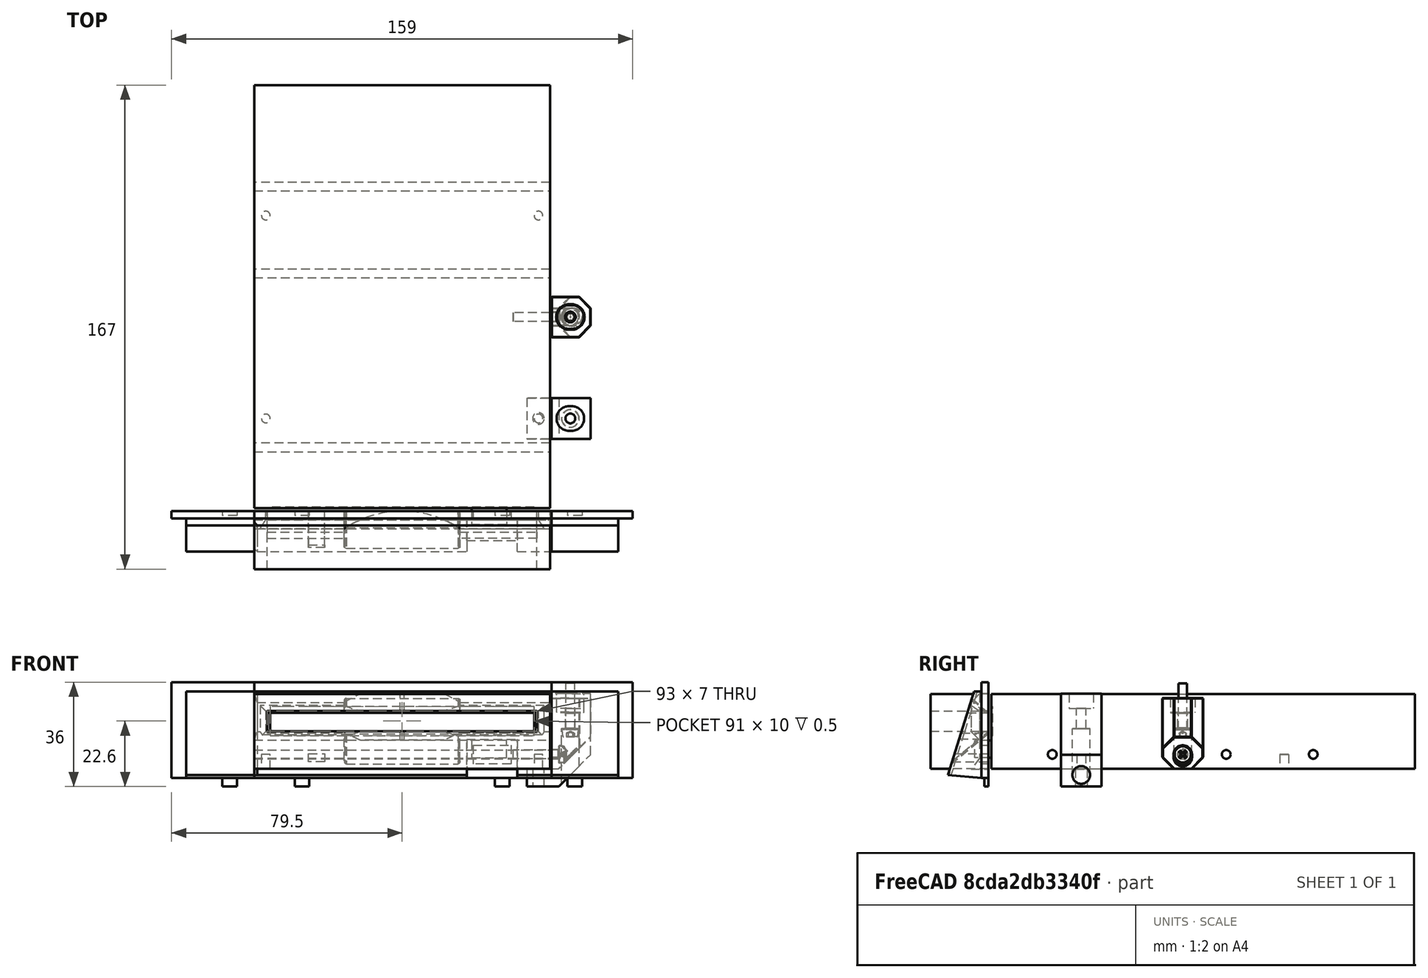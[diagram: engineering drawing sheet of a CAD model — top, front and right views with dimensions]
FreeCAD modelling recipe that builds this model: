
FCSTD DOCUMENT  (FreeCAD 0.21R33771 (Git))
Label: FDD
License: All rights reserved
LicenseURL: https://en.wikipedia.org/wiki/All_rights_reserved
objects: Sketcher::SketchObject×18, PartDesign::Pocket×10, Part::FeaturePython×8, PartDesign::Pad×6, PartDesign::Body×6, PartDesign::CoordinateSystem×6, PartDesign::Chamfer×6, PartDesign::Hole×3, PartDesign::LinearPattern×2, Part::Feature×2, PartDesign::Plane×2, App::DocumentObjectGroup×2, Mesh::Feature×1, PartDesign::FeatureBase×1
note: 95 computed .brp shape members not serialized (recipe doc carries the construction recipe); baked Part::Feature solids carry a one-line shape summary decoded from their .brp

FEATURE [Sketcher::SketchObject] Sketch  label="FloppyOutline"
  FullyConstrained = true
  MapMode = 5
  sketch-geometry (5):
    g0: LineSegment StartX=-51 StartY=73 StartZ=0 EndX=-51 EndY=-73 EndZ=0
    g1: LineSegment StartX=-51 StartY=-73 StartZ=0 EndX=51 EndY=-73 EndZ=0
    g2: LineSegment StartX=51 StartY=-73 StartZ=0 EndX=51 EndY=73 EndZ=0
    g3: LineSegment StartX=51 StartY=73 StartZ=0 EndX=-51 EndY=73 EndZ=0
    g4: GeomPoint X=0 Y=0 Z=0
  constraints (13):
    c: Coincident(g0,g1)
    c: Coincident(g1,g2)
    c: Coincident(g2,g3)
    c: Coincident(g3,g0)
    c: Vertical(g0)
    c: Vertical(g2)
    c: Horizontal(g1)
    c: Horizontal(g3)
    c: Symmetric(g2,g0,g4)
    c: Coincident(g4,g-1)
    c: DistanceX(g3,g3) = 102
    c: DistanceY(g2,g2) = 146
    c: Block(g2)
FEATURE [PartDesign::LinearPattern] LinearPattern
  Direction = -> X_Axis
  Length = 60
  Occurrences = 2
  Refine = true
  Reversed = true
FEATURE [PartDesign::LinearPattern] LinearPattern001
  BaseFeature = -> LinearPattern
  Direction = -> X_Axis
  Length = 90
  Occurrences = 2
  Refine = true
  Reversed = true
FEATURE [Sketcher::SketchObject] Sketch005
  AttachmentOffset = pos=(0,0,2) rot=(0,0,1;0rad)
  FullyConstrained = true
  MapMode = 5
  Placement = pos=(0,-2,-4e-16) rot=(1,0,0;1.5708rad)
  Support = -> [XZ_Plane001]
  sketch-geometry (7):
    g0: LineSegment StartX=43 StartY=-13 StartZ=0 EndX=43 EndY=-19 EndZ=0
    g1: LineSegment StartX=43 StartY=-19 StartZ=0 EndX=54 EndY=-19 EndZ=0
    g2: LineSegment StartX=54 StartY=-19 StartZ=0 EndX=65 EndY=-8 EndZ=0
    g3: LineSegment StartX=65 StartY=-8 StartZ=0 EndX=65 EndY=13 EndZ=0
    g4: LineSegment StartX=65 StartY=13 StartZ=0 EndX=51.5 EndY=13 EndZ=0
    g5: LineSegment StartX=51.5 StartY=13 StartZ=0 EndX=51.5 EndY=-13 EndZ=0
    g6: LineSegment StartX=51.5 StartY=-13 StartZ=0 EndX=43 EndY=-13 EndZ=0
  constraints (16):
    c: Coincident(g0,g1)
    c: Coincident(g3,g4)
    c: Coincident(g6,g0)
    c: Horizontal(g6)
    c: Parallel(g1,g-1)
    c: Coincident(g1,g2)
    c: Coincident(g4,g5)
    c: Coincident(g5,g6)
    c: Parallel(g4,g-1)
    c: Block(g5)
    c: Coincident(g2,g3)
    c: Angle(g-1,g2) = 0.785398
    c: Parallel(g3,g-2)
    c: Block(g4)
    c: Block(g2)
    c: Block(g0)
FEATURE [PartDesign::Pad] Pad002  label="Pad003"
  Direction = (0,-1,-2e-16)
  Length = 14
  Length2 = 10
  Midplane = true
  Placement = pos=(0,0,0) rot=(1,0,0;1.5708rad)
  Profile = -> Sketch005
  ReferenceAxis = -> Sketch005 [N_Axis]
  Refine = true
  Type = 0
FEATURE [Sketcher::SketchObject] Sketch007
  FullyConstrained = true
  MapMode = 5
  Placement = pos=(0,0,-19) rot=(1,0,0;3.14159rad)
  Support = -> [Pad002]
  sketch-geometry (1):
    g0: Circle CenterX=47 CenterY=2 CenterZ=0 NormalX=0 NormalY=0 NormalZ=1 AngleXU=0 Radius=2
  constraints (2):
    c: Block(g0)
    c: Diameter(g0) = 4
FEATURE [Sketcher::SketchObject] Sketch008
  FullyConstrained = true
  MapMode = 5
  Placement = pos=(2e-15,-3e-15,13) rot=(0,0,1;3.14159rad)
  sketch-geometry (4):
    g0: ArcOfCircle CenterX=-57.5013 CenterY=2 CenterZ=0 NormalX=0 NormalY=0 NormalZ=1 AngleXU=0 Radius=4.25 StartAngle=4.71239 EndAngle=7.85398
    g1: ArcOfCircle CenterX=-58.5 CenterY=2 CenterZ=0 NormalX=0 NormalY=0 NormalZ=1 AngleXU=0 Radius=4.25 StartAngle=1.5708 EndAngle=4.71239
    g2: LineSegment StartX=-57.5013 StartY=6.25 StartZ=0 EndX=-58.5 EndY=6.25 EndZ=0
    g3: LineSegment StartX=-58.5 StartY=-2.25 StartZ=0 EndX=-57.5013 EndY=-2.25 EndZ=0
  constraints (9):
    c: Tangent(g0,g2) = -1.5708
    c: Tangent(g2,g1) = -1.5708
    c: Tangent(g1,g3) = -1.5708
    c: Tangent(g3,g0) = -1.5708
    c: Equal(g0,g1)
    c: Horizontal(g2)
    c: Diameter(g1) = 8.5
    c: Block(g1)
    c: Block(g0)
FEATURE [PartDesign::Pocket] Pocket003
  BaseFeature = -> Pad002
  Direction = (0,0,-1)
  Length = 5
  Length2 = 5
  Placement = pos=(0,0,0) rot=(1,0,0;1.5708rad)
  Profile = -> Sketch008
  ReferenceAxis = -> Sketch008 [N_Axis]
  Refine = true
  Type = 0
FEATURE [Sketcher::SketchObject] Sketch009
  FullyConstrained = true
  MapMode = 5
  Placement = pos=(0,0,-19) rot=(1,0,0;3.14159rad)
  Support = -> [Pocket003]
  sketch-geometry (1):
    g0: Circle CenterX=58 CenterY=2 CenterZ=0 NormalX=0 NormalY=0 NormalZ=1 AngleXU=0 Radius=1.52384
  constraints (1):
    c: Block(g0)
FEATURE [PartDesign::Hole] Hole
  BaseFeature = -> Pocket003
  CustomThreadClearance = 0
  Depth = 81.8287
  DepthType = 1
  Diameter = 3.4
  DrillForDepth = false
  DrillPoint = 1
  DrillPointAngle = 118
  HoleCutCountersinkAngle = 90
  HoleCutCustomValues = false
  HoleCutDepth = 20
  HoleCutDiameter = 6.1
  HoleCutType = 1
  ModelThread = false
  Placement = pos=(0,0,0) rot=(1,0,0;1.5708rad)
  Profile = -> Sketch009
  Refine = true
  Tapered = false
  TaperedAngle = 90
  ThreadClass = 0
  ThreadDepth = 81.8287
  ThreadDepthType = 0
  ThreadDirection = 0
  ThreadFit = 0
  ThreadSize = 9
  ThreadType = 1
  Threaded = false
  UseCustomThreadClearance = false
FEATURE [PartDesign::Pocket] Pocket004  label="MountHole"
  BaseFeature = -> Hole
  Direction = (0,-2e-16,1)
  Length = 0
  Length2 = 5
  Placement = pos=(0,0,0) rot=(1,0,0;1.5708rad)
  Profile = -> Sketch007
  ReferenceAxis = -> Sketch007 [N_Axis]
  Refine = true
  Type = 2
FEATURE [PartDesign::Body] Body001  label="BottomBracket"
  Group = -> [Sketch005,Pad002,Sketch007,Sketch008,Pocket003,Sketch009,Hole,Pocket004]
  Origin = -> Origin001
  Placement = pos=(0,-40,0) rot=(0,0,1;0rad)
  Tip = -> Pocket004
FEATURE [PartDesign::Pad] Pad  label="FloppyCase"
  Direction = (0,0,1)
  Length = 25.8
  Length2 = 10
  Midplane = true
  Profile = -> Sketch
  ReferenceAxis = -> Sketch [N_Axis]
  Refine = true
  Type = 0
FEATURE [Sketcher::SketchObject] Sketch003  label="EjectSketch"
  FullyConstrained = true
  MapMode = 5
  Placement = pos=(0,-73,0) rot=(1,0,0;1.5708rad)
  Support = -> [Pad]
  sketch-geometry (5):
    g0: LineSegment StartX=24 StartY=-3.1 StartZ=0 EndX=24 EndY=-9.1 EndZ=0
    g1: LineSegment StartX=24 StartY=-9.1 StartZ=0 EndX=36 EndY=-9.1 EndZ=0
    g2: LineSegment StartX=36 StartY=-9.1 StartZ=0 EndX=36 EndY=-3.1 EndZ=0
    g3: LineSegment StartX=36 StartY=-3.1 StartZ=0 EndX=24 EndY=-3.1 EndZ=0
    g4: GeomPoint X=30 Y=-6.1 Z=0
  constraints (13):
    c: Coincident(g0,g1)
    c: Coincident(g1,g2)
    c: Coincident(g2,g3)
    c: Coincident(g3,g0)
    c: Vertical(g0)
    c: Vertical(g2)
    c: Horizontal(g1)
    c: Horizontal(g3)
    c: Symmetric(g2,g0,g4)
    c: DistanceX(g1,g1) = 12
    c: DistanceY(g2,g2) = 6
    c: DistanceX(g-1,g4) = 30
    c: DistanceY(g4) = -6.1
FEATURE [Sketcher::SketchObject] Sketch004  label="ShutterSketch"
  FullyConstrained = false
  MapMode = 5
  Placement = pos=(0,-73,0) rot=(1,0,0;1.5708rad)
  Support = -> [Pad]
  sketch-geometry (5):
    g0: LineSegment StartX=-45.5 StartY=8.6 StartZ=0 EndX=-45.5 EndY=-1.4 EndZ=0
    g1: LineSegment StartX=-45.5 StartY=-1.4 StartZ=0 EndX=45.5 EndY=-1.4 EndZ=0
    g2: LineSegment StartX=45.5 StartY=-1.4 StartZ=0 EndX=45.5 EndY=8.6 EndZ=0
    g3: LineSegment StartX=45.5 StartY=8.6 StartZ=0 EndX=-45.5 EndY=8.6 EndZ=0
    g4: GeomPoint X=0 Y=3.6 Z=0
  constraints (12):
    c: Coincident(g0,g1)
    c: Coincident(g1,g2)
    c: Coincident(g2,g3)
    c: Coincident(g3,g0)
    c: Vertical(g0)
    c: Vertical(g2)
    c: Horizontal(g1)
    c: Horizontal(g3)
    c: Symmetric(g2,g0,g4)
    c: DistanceX(g3,g3) = 91
    c: DistanceY(g0,g0) = 10
    c: PointOnObject(g4,g-2)
FEATURE [Sketcher::SketchObject] Sketch010  label="SideM3Holes"
  ExternalGeometry = -> [Pad]
  FullyConstrained = true
  MapMode = 5
  Placement = pos=(51,0,0) rot=(0.57735,0.57735,0.57735;2.0944rad)
  Support = -> [Pad]
  sketch-geometry (3):
    g0: Circle CenterX=-52 CenterY=-7.9 CenterZ=0 NormalX=0 NormalY=0 NormalZ=1 AngleXU=0 Radius=1.5
    g1: Circle CenterX=8 CenterY=-7.9 CenterZ=0 NormalX=0 NormalY=0 NormalZ=1 AngleXU=0 Radius=1.5
    g2: Circle CenterX=38 CenterY=-7.9 CenterZ=0 NormalX=0 NormalY=0 NormalZ=1 AngleXU=0 Radius=1.5
  constraints (9):
    c: DistanceY(g-4,g0) = 5
    c: DistanceY(g-4,g1) = 5
    c: DistanceY(g-4,g2) = 5
    c: DistanceX(g0,g2) = 90
    c: Equal(g0,g2)
    c: Diameter(g0) = 3
    c: Equal(g1,g0)
    c: DistanceX(g0,g1) = 60
    c: Block(g0)
FEATURE [PartDesign::Pocket] Pocket  label="SideM3"
  BaseFeature = -> Pad
  Direction = (-1,0,0)
  Length = 5
  Length2 = 5
  Profile = -> Sketch010
  ReferenceAxis = -> Sketch010 [N_Axis]
  Refine = true
  Type = 2
FEATURE [Sketcher::SketchObject] Sketch012  label="BottomM3"
  ExternalGeometry = -> [Pocket]
  FullyConstrained = true
  MapMode = 5
  Placement = pos=(0,0,-12.9) rot=(1,0,0;3.14159rad)
  Support = -> [Pocket]
  sketch-geometry (4):
    g0: Circle CenterX=-47 CenterY=42 CenterZ=0 NormalX=0 NormalY=0 NormalZ=1 AngleXU=0 Radius=1.5
    g1: Circle CenterX=47 CenterY=42 CenterZ=0 NormalX=0 NormalY=0 NormalZ=1 AngleXU=0 Radius=1.5
    g2: Circle CenterX=-47 CenterY=-28 CenterZ=0 NormalX=0 NormalY=0 NormalZ=1 AngleXU=0 Radius=1.5
    g3: Circle CenterX=47 CenterY=-28 CenterZ=0 NormalX=0 NormalY=0 NormalZ=1 AngleXU=0 Radius=1.5
  constraints (10):
    c: Diameter(g0) = 3
    c: Diameter(g1) = 3
    c: Diameter(g2) = 3
    c: Diameter(g3) = 3
    c: DistanceY(g0,g-3) = 31
    c: DistanceX(g0,g1) = 94
    c: Symmetric(g0,g1,g-2)
    c: Symmetric(g2,g3,g-2)
    c: DistanceX(g2,g3) = 94
    c: DistanceY(g2,g0) = 70
FEATURE [PartDesign::Pocket] Pocket005  label="BottomM004"
  BaseFeature = -> Pocket
  Direction = (0,0,1)
  Length = 5
  Length2 = 5
  Profile = -> Sketch012
  ReferenceAxis = -> Sketch012 [N_Axis]
  Refine = true
  Type = 0
FEATURE [Sketcher::SketchObject] Sketch013
  FullyConstrained = true
  MapMode = 5
  Placement = pos=(0,0,0) rot=(1,0,0;1.5708rad)
  Support = -> [XZ_Plane002]
  sketch-geometry (5):
    g0: LineSegment StartX=51.5 StartY=11.5 StartZ=0 EndX=65 EndY=11.5 EndZ=0
    g1: LineSegment StartX=65 StartY=11.5 StartZ=0 EndX=65 EndY=-1.9 EndZ=0
    g2: LineSegment StartX=65 StartY=-1.9 StartZ=0 EndX=54 EndY=-12.9 EndZ=0
    g3: LineSegment StartX=51.5 StartY=-12.9 StartZ=0 EndX=51.5 EndY=11.5 EndZ=0
    g4: LineSegment StartX=51.5 StartY=-12.9 StartZ=0 EndX=54 EndY=-12.9 EndZ=0
  constraints (14):
    c: Horizontal(g0)
    c: Coincident(g0,g1)
    c: Vertical(g1)
    c: Coincident(g1,g2)
    c: Coincident(g3,g0)
    c: Vertical(g3)
    c: Angle(g-1,g2) = 0.785398
    c: Coincident(g4,g3)
    c: Horizontal(g4)
    c: Coincident(g2,g4)
    c: DistanceX(g0,g0) = 13.5
    c: Block(g4)
    c: Block(g3)
    c: DistanceY(g3,g3) = 24.4
FEATURE [PartDesign::Pad] Pad003  label="Pad004"
  Direction = (0,-1,-2e-16)
  Length = 14
  Length2 = 10
  Placement = pos=(0,0,0) rot=(1,0,0;1.5708rad)
  Profile = -> Sketch013
  ReferenceAxis = -> Sketch013 [N_Axis]
  Refine = true
  Type = 0
FEATURE [Sketcher::SketchObject] Sketch014
  FullyConstrained = true
  MapMode = 5
  Placement = pos=(0,0,11.5) rot=(0,0,1;3.14159rad)
  Support = -> [Pad003]
  sketch-geometry (4):
    g0: ArcOfCircle CenterX=-58.5 CenterY=7 CenterZ=0 NormalX=0 NormalY=0 NormalZ=1 AngleXU=0 Radius=4.25 StartAngle=1.5708 EndAngle=4.71239
    g1: ArcOfCircle CenterX=-57.5 CenterY=7 CenterZ=0 NormalX=0 NormalY=0 NormalZ=1 AngleXU=0 Radius=4.25 StartAngle=4.71239 EndAngle=7.85398
    g2: LineSegment StartX=-58.5 StartY=2.75 StartZ=0 EndX=-57.5 EndY=2.75 EndZ=0
    g3: LineSegment StartX=-57.5 StartY=11.25 StartZ=0 EndX=-58.5 EndY=11.25 EndZ=0
  constraints (9):
    c: Tangent(g0,g2) = -1.5708
    c: Tangent(g2,g1) = -1.5708
    c: Tangent(g1,g3) = -1.5708
    c: Tangent(g3,g0) = -1.5708
    c: Equal(g0,g1)
    c: Horizontal(g2)
    c: Diameter(g0) = 8.5
    c: Block(g0)
    c: Block(g1)
FEATURE [PartDesign::Pocket] Pocket006
  BaseFeature = -> Pad003
  Direction = (0,2e-16,-1)
  Length = 5
  Length2 = 5
  Placement = pos=(0,0,0) rot=(1,0,0;1.5708rad)
  Profile = -> Sketch014
  ReferenceAxis = -> Sketch014 [N_Axis]
  Refine = true
  Type = 0
FEATURE [Sketcher::SketchObject] Sketch015
  FullyConstrained = true
  MapMode = 5
  Placement = pos=(0,0,-12.9) rot=(1,0,0;3.14159rad)
  Support = -> [Pocket006]
  sketch-geometry (1):
    g0: Circle CenterX=58 CenterY=7 CenterZ=0 NormalX=0 NormalY=0 NormalZ=1 AngleXU=0 Radius=1.5006
  constraints (1):
    c: Block(g0)
FEATURE [PartDesign::Hole] Hole001
  BaseFeature = -> Pocket006
  CustomThreadClearance = 0
  Depth = 25
  DepthType = 0
  Diameter = 3.4
  DrillForDepth = false
  DrillPoint = 1
  DrillPointAngle = 118
  HoleCutCountersinkAngle = 90
  HoleCutCustomValues = false
  HoleCutDepth = 14
  HoleCutDiameter = 6.1
  HoleCutType = 1
  ModelThread = false
  Placement = pos=(0,0,0) rot=(1,0,0;1.5708rad)
  Profile = -> Sketch015
  Refine = true
  Tapered = false
  TaperedAngle = 90
  ThreadClass = 0
  ThreadDepth = 25
  ThreadDepthType = 0
  ThreadDirection = 0
  ThreadFit = 0
  ThreadSize = 9
  ThreadType = 1
  Threaded = false
  UseCustomThreadClearance = false
FEATURE [Sketcher::SketchObject] Sketch016
  AttachmentOffset = pos=(0,0,65) rot=(0,0,1;0rad)
  FullyConstrained = true
  MapMode = 5
  Placement = pos=(65,-1.44e-14,1.44e-14) rot=(0.57735,0.57735,0.57735;2.0944rad)
  Support = -> [YZ_Plane002]
  sketch-geometry (2):
    g0: Circle CenterX=-7 CenterY=-7.9 CenterZ=0 NormalX=0 NormalY=0 NormalZ=1 AngleXU=0 Radius=1.5
    g1: LineSegment StartX=8 StartY=-7.9 StartZ=0 EndX=-14.3565 EndY=-7.9 EndZ=0
  constraints (5):
    c: Diameter(g0) = 3
    c: Horizontal(g1)
    c: PointOnObject(g0,g1)
    c: Block(g0)
    c: Block(g1)
FEATURE [PartDesign::Hole] Hole002
  BaseFeature = -> Hole001
  CustomThreadClearance = 0
  Depth = 25
  DepthType = 0
  Diameter = 3.4
  DrillForDepth = false
  DrillPoint = 1
  DrillPointAngle = 118
  HoleCutCountersinkAngle = 90
  HoleCutCustomValues = false
  HoleCutDepth = 11
  HoleCutDiameter = 6.1
  HoleCutType = 1
  ModelThread = false
  Placement = pos=(0,0,0) rot=(1,0,0;1.5708rad)
  Profile = -> Sketch016
  Refine = true
  Tapered = false
  TaperedAngle = 90
  ThreadClass = 0
  ThreadDepth = 25
  ThreadDepthType = 0
  ThreadDirection = 0
  ThreadFit = 0
  ThreadSize = 9
  ThreadType = 1
  Threaded = false
  UseCustomThreadClearance = false
FEATURE [PartDesign::CoordinateSystem] Local_CS  label="FrontRightLCS"
  AttacherType = Attacher::AttachEngine3D
  MapMode = 11
  Placement = pos=(51,-52,-7.9) rot=(0.707107,0,0.707107;3.14159rad)
  Support = -> [Pocket005]
FEATURE [PartDesign::CoordinateSystem] Local_CS001  label="BackRightLCS"
  AttacherType = Attacher::AttachEngine3D
  MapMode = 11
  Placement = pos=(51,38,-7.9) rot=(0.707107,0,0.707107;3.14159rad)
  Support = -> [Pocket005]
FEATURE [PartDesign::CoordinateSystem] Local_CS003  label="FloppyLCS"
  AttacherType = Attacher::AttachEngine3D
  MapMode = 11
  Placement = pos=(51.5,-7,-7.9) rot=(0.707107,0,-0.707107;3.14159rad)
  Support = -> [Hole002]
FEATURE [PartDesign::CoordinateSystem] Local_CS004  label="TopLidLCS"
  AttacherType = Attacher::AttachEngine3D
  MapMode = 11
  Placement = pos=(58,-7,6.5) rot=(0,0,-1;1.5708rad)
  Support = -> [Hole002]
FEATURE [PartDesign::CoordinateSystem] Local_CS005  label="FrontLeftLCS"
  AttacherType = Attacher::AttachEngine3D
  MapMode = 11
  Placement = pos=(-51,-52,-7.9) rot=(0.707107,0,0.707107;3.14159rad)
  Support = -> [Pocket005]
FEATURE [PartDesign::CoordinateSystem] Local_CS006  label="BackLeftLCS"
  AttacherType = Attacher::AttachEngine3D
  MapMode = 11
  Placement = pos=(-51,38,-7.9) rot=(0.707107,0,0.707107;3.14159rad)
  Support = -> [Pocket005]
FEATURE [PartDesign::Pad] Pad004  label="EjectButton"
  BaseFeature = -> Pocket005
  Direction = (0,-1,2e-16)
  Length = 5.7
  Length2 = 10
  Profile = -> Sketch003
  ReferenceAxis = -> Sketch003 [N_Axis]
  Refine = true
  Type = 0
FEATURE [PartDesign::Pocket] Pocket007  label="Shutter"
  BaseFeature = -> Pad004
  Direction = (0,1,-2e-16)
  Length = 0.5
  Length2 = 5
  Profile = -> Sketch004
  ReferenceAxis = -> Sketch004 [N_Axis]
  Refine = true
  Type = 0
FEATURE [PartDesign::Body] Body
  Group = -> [Sketch,LinearPattern,LinearPattern001,Sketch003,Sketch004,Pad,Sketch010,Pocket,Sketch012,Pocket005,Local_CS,Local_CS001,Local_CS005,Local_CS006,Pad004,Pocket007]
  Origin = -> Origin
  Tip = -> Pocket007
FEATURE [PartDesign::Chamfer] Chamfer
  Angle = 45
  Base = -> Hole002 [Edge16,Edge13]
  BaseFeature = -> Hole002
  ChamferType = 0
  FlipDirection = false
  Placement = pos=(0,0,0) rot=(1,0,0;1.5708rad)
  Refine = true
  Size = 4
  Size2 = 1
  SupportTransform = false
  UseAllEdges = false
FEATURE [Part::FeaturePython] Screw  label="M3x16-Screw"  # WARN: FeaturePython — macro-defined, semantics opaque (R4)
  Diameter = 4
  Invert = false
  LeftHanded = false
  Length = 7
  LengthCustom = 16
  MatchOuter = false
  OffsetAngle = 0
  Placement = pos=(58,-7,0.6) rot=(1,0,0;3.14159rad)
  Thread = false
  Type = 54
FEATURE [Part::FeaturePython] Screw001  label="M3x16-Screw001"  # WARN: FeaturePython — macro-defined, semantics opaque (R4)
  Diameter = 4
  Invert = false
  LeftHanded = false
  Length = 11
  LengthCustom = 16
  MatchOuter = false
  OffsetAngle = 0
  Placement = pos=(54.3,-7,-7.9) rot=(0,1,0;1.5708rad)
  Thread = false
  Type = 77
FEATURE [PartDesign::Chamfer] Chamfer001
  Angle = 45
  Base = -> Chamfer [Edge24,Edge14]
  BaseFeature = -> Chamfer
  ChamferType = 0
  FlipDirection = false
  Placement = pos=(0,0,0) rot=(1,0,0;1.5708rad)
  Refine = true
  Size = 4
  Size2 = 1
  SupportTransform = false
  UseAllEdges = false
FEATURE [PartDesign::Chamfer] Chamfer002
  Angle = 45
  Base = -> Chamfer001 [Edge1,Edge2,Edge3,Edge4,Edge5,Edge6,Edge7,Edge8,Edge9,Edge10,Edge11,Edge12,Edge13,Edge14,Edge15,Edge16,Edge17,Edge18,Edge19,Edge20,Edge21,Edge22,Edge23,Edge24,Edge25,Edge26,Edge27,Edge28,Edge29,Edge30,Edge31,Edge32,Edge33,Edge34,Edge35,Edge36,Edge37,Edge38,Edge39,Edge40,+21 more]
  BaseFeature = -> Chamfer001
  ChamferType = 0
  FlipDirection = false
  Placement = pos=(0,0,0) rot=(1,0,0;1.5708rad)
  Refine = true
  Size = 0.15
  Size2 = 1
  SupportTransform = false
  UseAllEdges = true
FEATURE [PartDesign::Body] Body002  label="SideBracket"
  Group = -> [Sketch013,Pad003,Sketch014,Pocket006,Sketch015,Hole001,Sketch016,Hole002,Local_CS003,Local_CS004,Chamfer,Chamfer001,Chamfer002]
  Origin = -> Origin002
  Tip = -> Chamfer002
FEATURE [Sketcher::SketchObject] Sketch017
  FullyConstrained = false
  MapMode = 5
  Placement = pos=(0,0,0) rot=(0.57735,0.57735,0.57735;2.0944rad)
  Support = -> [YZ_Plane003]
  sketch-geometry (12):
    g0: LineSegment StartX=-74 StartY=13 StartZ=0 EndX=-77 EndY=13 EndZ=0
    g1: LineSegment StartX=-77 StartY=13 StartZ=0 EndX=-80 EndY=10 EndZ=0
    g2: LineSegment StartX=-80 StartY=10 StartZ=0 EndX=-80 EndY=8 EndZ=0
    g3: LineSegment StartX=-80 StartY=8 StartZ=0 EndX=-80 EndY=7.36918 EndZ=0
    g4: LineSegment StartX=-80 StartY=7.36918 StartZ=0 EndX=-80 EndY=2.36918 EndZ=0
    g5: LineSegment StartX=-80 StartY=2.36918 StartZ=0 EndX=-80 EndY=1 EndZ=0
    g6: LineSegment StartX=-80 StartY=1 StartZ=0 EndX=-80 EndY=0 EndZ=0
    g7: LineSegment StartX=-80 StartY=0 StartZ=0 EndX=-77 EndY=-3 EndZ=0
    g8: LineSegment StartX=-77 StartY=-3 StartZ=0 EndX=-77 EndY=-9.20497 EndZ=0
    g9: LineSegment StartX=-77 StartY=-9.20497 StartZ=0 EndX=-80 EndY=-13 EndZ=0
    g10: LineSegment StartX=-80 StartY=-13 StartZ=0 EndX=-74 EndY=-13 EndZ=0
    g11: LineSegment StartX=-74 StartY=-13 StartZ=0 EndX=-74 EndY=13 EndZ=0
  constraints (19):
    c: Horizontal(g0)
    c: Coincident(g0,g1)
    c: Coincident(g1,g2)
    c: Vertical(g2)
    c: Coincident(g2,g3)
    c: Coincident(g3,g4)
    c: Vertical(g4)
    c: Coincident(g4,g5)
    c: Coincident(g5,g6)
    c: PointOnObject(g6,g-1)
    c: Coincident(g6,g7)
    c: Coincident(g7,g8)
    c: Vertical(g8)
    c: Coincident(g8,g9)
    c: Coincident(g9,g10)
    c: Horizontal(g10)
    c: Coincident(g10,g11)
    c: Coincident(g11,g0)
    c: Vertical(g11)
FEATURE [PartDesign::Pad] Pad005
  Direction = (1,-2e-16,3e-16)
  Length = 102
  Length2 = 10
  Midplane = true
  Placement = pos=(0,0,0) rot=(0.57735,0.57735,0.57735;2.0944rad)
  Profile = -> Sketch017
  ReferenceAxis = -> Sketch017 [N_Axis]
  Refine = true
  Type = 0
FEATURE [Sketcher::SketchObject] Sketch018
  FullyConstrained = false
  MapMode = 5
  Placement = pos=(-3.44e-14,-80,0) rot=(0.57735,0.57735,-0.57735;2.0944rad)
  Support = -> [Pad005]
  sketch-geometry (4):
    g0: LineSegment StartX=-9 StartY=-49 StartZ=0 EndX=2 EndY=-49 EndZ=0
    g1: LineSegment StartX=2 StartY=-49 StartZ=0 EndX=2 EndY=49 EndZ=0
    g2: LineSegment StartX=2 StartY=49 StartZ=0 EndX=-9 EndY=49 EndZ=0
    g3: LineSegment StartX=-9 StartY=49 StartZ=0 EndX=-9 EndY=-49 EndZ=0
  constraints (8):
    c: Coincident(g0,g1)
    c: Coincident(g1,g2)
    c: Coincident(g2,g3)
    c: Coincident(g3,g0)
    c: Horizontal(g0)
    c: Horizontal(g2)
    c: Vertical(g1)
    c: Vertical(g3)
FEATURE [PartDesign::Pocket] Pocket008
  BaseFeature = -> Pad005
  Direction = (4e-16,1,-2e-16)
  Length = 3
  Length2 = 5
  Placement = pos=(0,0,0) rot=(0.57735,0.57735,0.57735;2.0944rad)
  Profile = -> Sketch018
  ReferenceAxis = -> Sketch018 [N_Axis]
  Refine = true
  TaperAngle = -33
  Type = 0
FEATURE [Sketcher::SketchObject] Sketch019
  ExternalGeometry = -> [Pocket008]
  FullyConstrained = false
  MapMode = 5
  Placement = pos=(-3.6e-15,5.7e-15,13) rot=(0,0,-1;1.5708rad)
  Support = -> [Pocket008]
  sketch-geometry (1):
    g0: Circle CenterX=110.15 CenterY=0 CenterZ=0 NormalX=0 NormalY=0 NormalZ=1 AngleXU=0 Radius=36.1558
  constraints (1):
    c: PointOnObject(g0,g-1)
FEATURE [PartDesign::Pocket] Pocket009
  BaseFeature = -> Pocket008
  Direction = (7e-16,-7e-16,-1)
  Length = 16
  Length2 = 5
  Placement = pos=(0,0,0) rot=(0.57735,0.57735,0.57735;2.0944rad)
  Profile = -> Sketch019
  ReferenceAxis = -> Sketch019 [N_Axis]
  Refine = true
  Type = 0
FEATURE [PartDesign::Chamfer] Chamfer003
  Angle = 45
  Base = -> Pocket009 [Edge55]
  BaseFeature = -> Pocket009
  ChamferType = 1
  FlipDirection = false
  Placement = pos=(0,0,0) rot=(0.57735,0.57735,0.57735;2.0944rad)
  Refine = true
  Size = 3
  Size2 = 1
  SupportTransform = false
  UseAllEdges = false
FEATURE [PartDesign::Chamfer] Chamfer004
  Angle = 45
  Base = -> Chamfer003 [Edge56]
  BaseFeature = -> Chamfer003
  ChamferType = 1
  FlipDirection = false
  Placement = pos=(0,0,0) rot=(0.57735,0.57735,0.57735;2.0944rad)
  Refine = true
  Size = 3
  Size2 = 1
  SupportTransform = false
  UseAllEdges = false
FEATURE [PartDesign::Pocket] Pocket010
  BaseFeature = -> Chamfer004
  Direction = (5e-16,1,1.9e-15)
  Length = 5
  Length2 = 5
  Placement = pos=(0,0,0) rot=(0.57735,0.57735,0.57735;2.0944rad)
  Profile = -> Pocket008 [Face15]
  Refine = true
  Type = 0
FEATURE [PartDesign::Body] Body003  label="FrontPanel"
  Group = -> [Sketch017,Pad005,Sketch018,Pocket008,Sketch019,Pocket009,Chamfer003,Chamfer004,Pocket010]
  Origin = -> Origin003
  Tip = -> Pocket010
FEATURE [Mesh::Feature] IBM_PS2_56_Type_9556_Floppy_Drive_Cover_92F1599___Cast_2540_Scale  label="IBM_PS2_56_Type_9556_Floppy_Drive_Cover_92F1599_-_Cast_2540_Scale"
FEATURE [Part::Feature] IBM_PS2_56_Type_9556_Floppy_Drive_Cover_92F1599___Cast_2540_Scale001
  Placement = pos=(0,-76.4,-1.1) rot=(1,0,0;1.5708rad)
  shape: bbox 159 x 14 x 36 mm, 246 faces, 0 solids (baked)
FEATURE [PartDesign::Plane] DatumPlane
  AttachmentOffset = pos=(0,9,-23) rot=(0,0,1;0rad)
  Length = 65.0299
  MapMode = 5
  Placement = pos=(51.5,-85.4,-1.1) rot=(0.707107,0,0.707107;3.14159rad)
  ResizeMode = 0
  Support = -> [IBM_PS2_56_Type_9556_Floppy_Drive_Cover_92F1599___Cast_2540_Scale001]
  Width = 127.979
FEATURE [Part::Feature] IBM_PS2_56_Type_9556_Floppy_Drive_Cover_92F1599___Cast_2540_Scale001_solid  label="IBM_PS2_56_Type_9556_Floppy_Drive_Cover_92F1599___Cast_2540_Scale001 (Solid)"
  shape: bbox 159 x 14 x 36 mm, 246 faces (baked)
FEATURE [Part::FeaturePython] Slice  # WARN: FeaturePython — macro-defined, semantics opaque (R4)
  Base = -> IBM_PS2_56_Type_9556_Floppy_Drive_Cover_92F1599___Cast_2540_Scale001_solid
  Mode = 1
  Tolerance = 0
  Tools = -> [DatumPlane]
FEATURE [Part::FeaturePython] Slice_child0  label="Slice.0"  # WARN: FeaturePython — macro-defined, semantics opaque (R4)
  Base = -> Slice
  FilterType = 1
  Invert = false
  OverrideMaxVal = 0
  WindowFrom = 80
  WindowTo = 100
  items = 0
FEATURE [Part::FeaturePython] Slice_child1  label="Slice.1"  # WARN: FeaturePython — macro-defined, semantics opaque (R4)
  Base = -> Slice
  FilterType = 1
  Invert = false
  OverrideMaxVal = 0
  WindowFrom = 80
  WindowTo = 100
  items = 1
FEATURE [App::DocumentObjectGroup] GrExplode_Slice  label="Exploded Slice"
  Group = -> [Slice_child0,Slice_child1]
FEATURE [PartDesign::Plane] DatumPlane001
  Length = 127.979
  MapMode = 5
  Placement = pos=(-51,0,0) rot=(0.57735,-0.57735,-0.57735;2.0944rad)
  ResizeMode = 0
  Support = -> [Pocket007]
  Width = 65.0299
FEATURE [Part::FeaturePython] Slice001  # WARN: FeaturePython — macro-defined, semantics opaque (R4)
  Base = -> Slice_child1
  Mode = 1
  Tolerance = 0
  Tools = -> [DatumPlane001]
FEATURE [Part::FeaturePython] Slice001_child0  label="Slice001.0"  # WARN: FeaturePython — macro-defined, semantics opaque (R4)
  Base = -> Slice001
  FilterType = 1
  Invert = false
  OverrideMaxVal = 0
  WindowFrom = 80
  WindowTo = 100
  items = 0
FEATURE [Part::FeaturePython] Slice001_child1  label="Slice001.1"  # WARN: FeaturePython — macro-defined, semantics opaque (R4)
  Base = -> Slice001
  FilterType = 1
  Invert = false
  OverrideMaxVal = 0
  WindowFrom = 80
  WindowTo = 100
  items = 1
FEATURE [App::DocumentObjectGroup] GrExplode_Slice001  label="Exploded Slice001"
  Group = -> [Slice001_child1]
FEATURE [PartDesign::FeatureBase] BaseFeature
  BaseFeature = -> Slice001_child0
FEATURE [PartDesign::Chamfer] Chamfer005
  Angle = 45
  Base = -> BaseFeature [Edge87]
  BaseFeature = -> BaseFeature
  ChamferType = 0
  FlipDirection = false
  Refine = true
  Size = 1
  Size2 = 1
  SupportTransform = false
  UseAllEdges = false
FEATURE [PartDesign::Body] Body004  label="IBM PS2"
  BaseFeature = -> Slice001_child0
  Group = -> [BaseFeature,DatumPlane,DatumPlane001,Chamfer005]
  Origin = -> Origin004
  Tip = -> Chamfer005
FEATURE [Sketcher::SketchObject] Sketch020
  AttachmentOffset = pos=(0,0,74) rot=(0,0,1;0rad)
  FullyConstrained = true
  MapMode = 5
  Placement = pos=(0,-74,1.64e-14) rot=(1,0,0;1.5708rad)
  Support = -> [XZ_Plane005]
  sketch-geometry (5):
    g0: LineSegment StartX=51 StartY=-12.9 StartZ=0 EndX=51 EndY=12.9 EndZ=0
    g1: LineSegment StartX=51 StartY=12.9 StartZ=0 EndX=-51 EndY=12.9 EndZ=0
    g2: LineSegment StartX=-51 StartY=12.9 StartZ=0 EndX=-51 EndY=-12.9 EndZ=0
    g3: LineSegment StartX=-51 StartY=-12.9 StartZ=0 EndX=51 EndY=-12.9 EndZ=0
    g4: GeomPoint X=0 Y=0 Z=0
  constraints (11):
    c: Coincident(g0,g1)
    c: Coincident(g1,g2)
    c: Coincident(g2,g3)
    c: Coincident(g3,g0)
    c: Horizontal(g1)
    c: Horizontal(g3)
    c: Vertical(g0)
    c: Vertical(g2)
    c: Symmetric(g1,g0,g4)
    c: Coincident(g4,g-1)
    c: Block(g1)
FEATURE [PartDesign::Pad] Pad006
  Direction = (0,-1,2e-16)
  Length = 20
  Length2 = 10
  Placement = pos=(0,0,0) rot=(1,0,0;1.5708rad)
  Profile = -> Sketch020
  ReferenceAxis = -> Sketch020 [N_Axis]
  Refine = true
  Type = 0
FEATURE [Sketcher::SketchObject] Sketch021
  FullyConstrained = true
  MapMode = 5
  Placement = pos=(0,-94,0) rot=(1,0,0;1.5708rad)
  Support = -> [Pad006]
  sketch-geometry (5):
    g0: LineSegment StartX=46.5 StartY=0.1 StartZ=0 EndX=46.5 EndY=7.1 EndZ=0
    g1: LineSegment StartX=46.5 StartY=7.1 StartZ=0 EndX=-46.5 EndY=7.1 EndZ=0
    g2: LineSegment StartX=-46.5 StartY=7.1 StartZ=0 EndX=-46.5 EndY=0.1 EndZ=0
    g3: LineSegment StartX=-46.5 StartY=0.1 StartZ=0 EndX=46.5 EndY=0.1 EndZ=0
    g4: GeomPoint X=0 Y=3.6 Z=0
  constraints (14):
    c: Coincident(g0,g1)
    c: Coincident(g1,g2)
    c: Coincident(g2,g3)
    c: Coincident(g3,g0)
    c: Horizontal(g1)
    c: Horizontal(g3)
    c: Vertical(g0)
    c: Vertical(g2)
    c: Symmetric(g1,g0,g4)
    c: Block(g0)
    c: Block(g3)
    c: PointOnObject(g4,g-2)
    c: DistanceX(g1,g1) = 93
    c: Block(g1)
FEATURE [PartDesign::Pocket] Pocket011
  BaseFeature = -> Pad006
  Direction = (0,1,-2e-16)
  Length = 20
  Length2 = 5
  Placement = pos=(0,0,0) rot=(1,0,0;1.5708rad)
  Profile = -> Sketch021
  ReferenceAxis = -> Sketch021 [N_Axis]
  Refine = true
  Type = 0
FEATURE [PartDesign::Body] Body005
  Group = -> [Sketch020,Sketch021,Pad006,Pocket011]
  Origin = -> Origin005
  Tip = -> Pocket011
